# Revit family: oventrop_cocon-qtz_1147504-7704rfa
name_source: partatom
category: Арматура трубопроводов
revit_build: Autodesk Revit 2017 (Build: 20160225_1515(x64)
units: mm (PartAtom-declared; Revit-internal decimal feet)

## family parameters
Всегда вертикально = Да
Заголовок OmniClass = Adjusting/Controlling Valves for Liquid Services
На основе рабочей плоскости = Нет
Номер OmniClass = 23.65.55.14.17
Общий = Нет
При загрузке вырезать с полостями = Нет
Размер круглого соединителя = Использовать радиус
Тип детали = Клапан - Вставляется

## types (7) — shared parameters
Angle = 75.00°
Article Description = Flow control valve - without pressure test points
Article Type = Cocon QTZ Female-Female 1147
Black = Color RGB 35-35-35
Brass = Color RGB 168-128-48
Custom = Нет
EMCS Version = 2.0
ETIM Article Class = EC011435
Family Version = 10.14
H3 = 4.42 мм
Hb2 = 7 мм
Hb3 = 15 мм
Hb4 = 5 мм
Hb5 = 10 мм
Hb6 = 6 мм
Hb7 = 2 мм
Hb8 = 2 мм
Hb9 = 17 мм
IFCExportAs = IfcValveType
IFCExportType = REGULATING
Lb2 = 5 мм
Lb3 = 1.5 мм
MEPcontent Class = VALVE_CONTROL
Manufacturer URL = http://www.oventrop.de
Plastic Red = Color RGB 255-0-0
Pressure Drop = 0.0 Па
Product Line = Oventrop
Rb3 = 9 мм
Rb4 = 16.5 мм
Rb5 = 17.5 мм
Revit Version = 2015
Rv1 = 6 мм
Rv2 = 9.4 мм
Rv3 = 7.7 мм
d1 = 5 мм
d2 = 2 мм
r1 = 1 мм
r2 = 2 мм
Группа модели = Cocon QTZ Female-Female 1147
Изготовитель = Oventrop
Описание = Flow control valve - without pressure test points

## per-type parameters (varying)
- DN 20 (150-1050): Arrow_1=4.63 мм; Arrow_2=3.08 мм; GTIN=4026755394856; H4=49.4 мм; H5=4.96 мм; H6=44.7 мм; Hb1=11.2 мм; Height=52 мм; Height1=52 мм; Height2=48 мм; L1_2=54.9 мм; L2=78 мм; L3=15.24 мм; L4=18.1 мм; L5=18.1 мм; LMx=38.25 мм; Lb1=9.25 мм; Lb8=13 мм; Length=78 мм; Manufacturer Art. No.=1147506; NominalDiameter1=19.05 мм; NominalDiameter2=19.05 мм; OuterDiameter1=26.9 мм; OuterDiameter2=26.9 мм; Ra1=10 мм; Ra1b=9 мм; Ra2=10.48 мм; Rb1=18.5 мм; Rb1b=19.5 мм; Rb2=21.83 мм; SW1_1=30 мм; SW1_2=30 мм; SW2_1=34.64 мм; SW2_1_05=17.32 мм; SW2_1_051=40 мм; SW2_2=34.64 мм; URL=www.stabiplan.com; r3=4.52 мм
- DN 15 (30-210): Arrow_1=4.63 мм; Arrow_2=3.08 мм; GTIN=4026755394849; H4=49.4 мм; H5=4.96 мм; H6=44.7 мм; Hb1=11.2 мм; Height=52 мм; Height1=52 мм; Height2=48 мм; L1_2=57.44 мм; L2=74.5 мм; L3=10.16 мм; L4=12.07 мм; L5=12.07 мм; LMx=32.22 мм; Lb1=9.25 мм; Lb8=13 мм; Length=74.5 мм; Manufacturer Art. No.=1147504; NominalDiameter1=12.70 мм; NominalDiameter2=12.70 мм; OuterDiameter1=21.3 мм; OuterDiameter2=21.3 мм; Ra1=7.5 мм; Ra1b=6.5 мм; Ra2=6.99 мм; Rb1=18.5 мм; Rb1b=19.5 мм; Rb2=21.83 мм; SW1_1=24 мм; SW1_2=24 мм; SW2_1=27.71 мм; SW2_1_05=13.86 мм; SW2_1_051=32 мм; SW2_2=27.71 мм; URL=www.stabiplan.com; r3=5.02 мм
- DN 20 (180-1300): Arrow_1=5.2 мм; Arrow_2=3.47 мм; GTIN=4026755394870; H4=55.6 мм; H5=5.58 мм; H6=50.9 мм; Hb1=14.3 мм; Height=58 мм; Height1=58 мм; Height2=54.5 мм; L1_2=65.9 мм; L2=89 мм; L3=15.24 мм; L4=18.1 мм; L5=18.1 мм; LMx=40.64 мм; Lb1=10.41 мм; Lb8=14.63 мм; Length=89 мм; Manufacturer Art. No.=1147606; NominalDiameter1=19.05 мм; NominalDiameter2=19.05 мм; OuterDiameter1=26.9 мм; OuterDiameter2=26.9 мм; Ra1=10 мм; Ra1b=9 мм; Ra2=10.48 мм; Rb1=20.81 мм; Rb1b=21.81 мм; Rb2=24.15 мм; SW1_1=30 мм; SW1_2=30 мм; SW2_1=34.64 мм; SW2_1_05=17.32 мм; SW2_1_051=40 мм; SW2_2=34.64 мм; URL=www.stabiplan.com; r3=4.52 мм
- DN 25 (300-2000): Arrow_1=6.71 мм; Arrow_2=4.47 мм; GTIN=4026755394887; H4=63.8 мм; H5=7.19 мм; H6=74.6 мм; Hb1=18.4 мм; Height=66 мм; Height1=66 мм; Height2=79 мм; L1_2=92.87 мм; L2=122 мм; L3=20.32 мм; L4=24.13 мм; L5=24.13 мм; LMx=52.9 мм; Lb1=13.41 мм; Lb8=18.85 мм; Length=122 мм; Manufacturer Art. No.=1147608; NominalDiameter1=25.40 мм; NominalDiameter2=25.40 мм; OuterDiameter1=33.7 мм; OuterDiameter2=33.7 мм; Ra1=12.5 мм; Ra1b=11.5 мм; Ra2=13.97 мм; Rb1=26.83 мм; Rb1b=27.83 мм; Rb2=30.16 мм; SW1_1=36 мм; SW1_2=36 мм; SW2_1=41.57 мм; SW2_1_05=20.78 мм; SW2_1_051=48 мм; SW2_2=41.57 мм; URL=www.stabiplan.com; r3=4.03 мм
- DN 32 (600-3600): Arrow_1=6.71 мм; Arrow_2=4.47 мм; GTIN=4026755394894; H4=63.8 мм; H5=7.19 мм; H6=74.6 мм; Hb1=18.4 мм; Height=66 мм; Height1=66 мм; Height2=79 мм; L1_2=94.84 мм; L2=130 мм; L3=25.4 мм; L4=30.16 мм; L5=30.16 мм; LMx=58.93 мм; Lb1=13.41 мм; Lb8=18.85 мм; Length=130 мм; Manufacturer Art. No.=1147610; NominalDiameter1=31.75 мм; NominalDiameter2=31.75 мм; OuterDiameter1=42.4 мм; OuterDiameter2=42.4 мм; Ra1=16 мм; Ra1b=15 мм; Ra2=17.46 мм; Rb1=26.83 мм; Rb1b=27.83 мм; Rb2=30.16 мм; SW1_1=45 мм; SW1_2=45 мм; SW2_1=51.96 мм; SW2_1_05=25.98 мм; SW2_1_051=60 мм; SW2_2=51.96 мм; URL=http://file-system.ru; r3=5.04 мм
- DN 15 (90-450): Arrow_1=4.63 мм; Arrow_2=3.08 мм; GTIN=4026755394863; H4=49.4 мм; H5=4.96 мм; H6=44.7 мм; Hb1=11.2 мм; Height=52 мм; Height1=52 мм; Height2=48 мм; L1_2=57.44 мм; L2=74.5 мм; L3=10.16 мм; L4=12.07 мм; L5=12.07 мм; LMx=32.22 мм; Lb1=9.25 мм; Lb8=13 мм; Length=74.5 мм; Manufacturer Art. No.=1147604; NominalDiameter1=12.70 мм; NominalDiameter2=12.70 мм; OuterDiameter1=21.3 мм; OuterDiameter2=21.3 мм; Ra1=7.5 мм; Ra1b=6.5 мм; Ra2=6.99 мм; Rb1=18.5 мм; Rb1b=19.5 мм; Rb2=21.83 мм; SW1_1=24 мм; SW1_2=24 мм; SW2_1=27.71 мм; SW2_1_05=13.86 мм; SW2_1_051=32 мм; SW2_2=27.71 мм; URL=www.stabiplan.com; r3=5.02 мм
- DN 15 (150-1050): Arrow_1=4.63 мм; Arrow_2=3.08 мм; GTIN=4026755394900; H4=49.4 мм; H5=4.96 мм; H6=44.7 мм; Hb1=11.2 мм; Height=52 мм; Height1=52 мм; Height2=48 мм; L1_2=57.44 мм; L2=74.5 мм; L3=10.16 мм; L4=12.07 мм; L5=12.07 мм; LMx=32.22 мм; Lb1=9.25 мм; Lb8=13 мм; Length=74.5 мм; Manufacturer Art. No.=1147704; NominalDiameter1=12.70 мм; NominalDiameter2=12.70 мм; OuterDiameter1=21.3 мм; OuterDiameter2=21.3 мм; Ra1=7.5 мм; Ra1b=6.5 мм; Ra2=6.99 мм; Rb1=18.5 мм; Rb1b=19.5 мм; Rb2=21.83 мм; SW1_1=24 мм; SW1_2=24 мм; SW2_1=27.71 мм; SW2_1_05=13.86 мм; SW2_1_051=32 мм; SW2_2=27.71 мм; URL=www.stabiplan.com; r3=5.02 мм

## geometry (parser evidence)
native form markers: Blend x2, Sweep x3
no freeform markers — native parametric forms only
